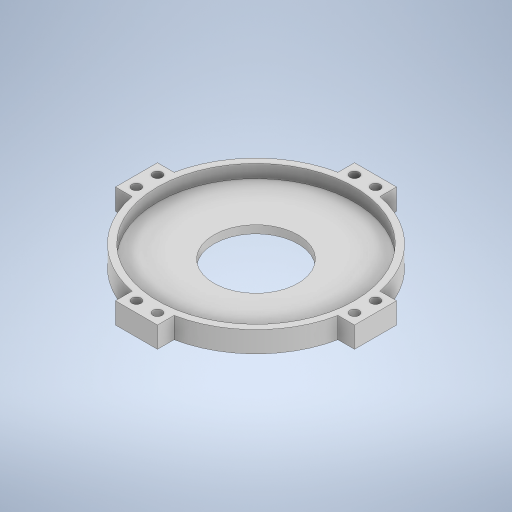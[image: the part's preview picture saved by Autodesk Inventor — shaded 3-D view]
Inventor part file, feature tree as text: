
AUTODESK INVENTOR PART (.ipt)
format: ipt  version: 2023 (Build 270158000, 158)  size: 334,848 bytes
history: native  units: in
note: dims shown in document units (in); Inventor stores cm internally (conversion verified against a paired STEP export)
features: extrude x4, sketch x4
ambient origin geometry x8: Origin, YZ Plane, XZ Plane, XY Plane, X Axis, Y Axis, Z Axis, Center Point
bodies: Solid1 (feature_tree)
feature tree (8):
  extrude  "Extrusion1"  Depth=1.6in
  extrude  "Extrusion2"  Depth=0.4in
  extrude  "Extrusion3"  Depth=0.4in
  extrude  "Extrusion4"  Depth=0.8in
  sketch  "Sketch1"  dims[d0=4.0in d1=1.6in]
  sketch  "Sketch2"  dims[d2=0.4in d3=0.0in d4=3.75in]
  sketch  "Sketch3"  dims[d5=0.25in d6=0.0in d7=0.4in]
  sketch  "Sketch4"  dims[d8=0.4in d9=0.8in d10=0.4in d11=0.4in d12=0.4in d13=0.8in d14=0.4in d15=0.4in d16=0.4in d17=0.8in d18=0.4in d19=0.4in d20=0.4in d21=0.4in d22=0.8in d23=0.4in d24=0.25in d25=0.0in d26=0.2in d27=0.2in d28=0.4in d29=0.2in d30=0.2in d31=0.4in d32=0.2in d33=0.2in d34=0.4in d35=0.2in d36=0.2in d37=0.4in d38=0.177in d39=0.177in d40=0.177in d41=0.177in d42=0.177in d43=0.177in d44=0.177in d45=1.0in d46=0.0in d47=0.5in d48=0.0344in d49=0.5in d50=0.0344in]
